# Revit family: Basin_Pedestal-Dee-DXV-Fitzgerald-D2001500x_D21015000_Series
name_source: partatom
category: Plumbing Fixtures
revit_build: Autodesk Revit 2014 (Build: 20130308_1515(x64)
units: mm (PartAtom-declared; Revit-internal decimal feet)

## types (4) — shared parameters
Assembly Code = D2010310
CW Connection = Yes
CWFU = 1.5
Cold Water Connection Height = 20 3/4"
Cold Water Connection Width = 4"
Cold Water Diameter = 1/2"
Cold Water Radius = 1/4"
Default Elevation = 36"
HW Connection = Yes
HWFU = 1.5
Height = 36"
Hot Water Connection Height = 20 3/4"
Hot Water Connection Width = 4"
Hot Water Diameter = 1/2"
Hot Water Radius = 1/4"
Installation Type = Floor Mounted
Length = 22"
Manufacturer = DXV
Product Documentation Link = https://dxv01.blob.core.windows.net
Product Page URL = https://www.dxv.com
URL = www.dxv.com
Vent Connection = No
WFU = 2
Waste Connection = Yes
Waste Connection Diameter = 1 1/4"
Waste Connection Height = 18 3/4"
Waste Connection Radius = 5/8"
Width = 28"

## per-type parameters (varying)
| type | Description | Finish | Hole Punch Location | Material | Model |
| D20015001.071-D21015000.071 | FITZGERALD 28 INCH PEDESTAL BATHROOM SINK- SINGLE FAUCET HOLE | Fire Clay-DXV-071-Biscuit | 50" | Fire Clay-DXV-071-Biscuit | D20015001.071, D21015000.071 |
| D20015001.415-D21015000.415 | FITZGERALD 28 INCH PEDESTAL BATHROOM SINK- SINGLE FAUCET HOLE | Fire Clay-DXV-415-Canvas White | 50" | Fire Clay-DXV-415-Canvas White | D20015001.415, D21015000.415 |
| D20015008.071-D21015000.071 | FITZGERALD 28 INCH PEDESTAL BATHROOM SINK- THREE FAUCET HOLES | Fire Clay-DXV-071-Biscuit | 8" | Fire Clay-DXV-071-Biscuit | D20015008.071, D21015000.071 |
| D20015008.415-D21015000.415 | FITZGERALD 28 INCH PEDESTAL BATHROOM SINK- THREE FAUCET HOLES | Fire Clay-DXV-415-Canvas White | 8" | Fire Clay-DXV-415-Canvas White | D20015008.415, D21015000.415 |

## geometry (parser evidence)
native form markers: Sweep x1
no freeform markers — native parametric forms only
